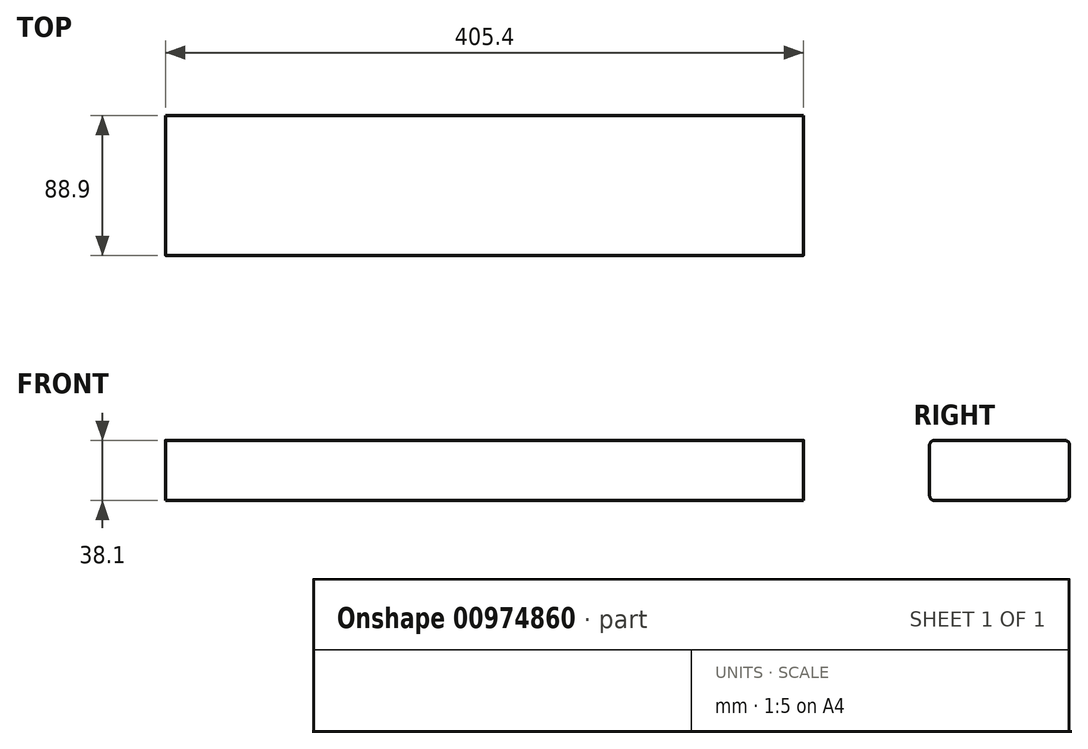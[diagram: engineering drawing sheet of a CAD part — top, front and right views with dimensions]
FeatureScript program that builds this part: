
annotation { "Feature Type Name" : "Feature", "Feature Type Description" : "" }
export const myFeature = defineFeature(function(context is Context, id is Id, definition is map)
    precondition{}
    {
        {
            var Q0;
            Q0=qCreatedBy(makeId("Top.planeOp"),FACE);
            var sketch = newSketch(context, id + "F0", { "sketchPlane" : qUnion([Q0])});
            skLineSegment(sketch, "E0.bottom", {"start": v(202.7, 44.45) * mm, "end": v(-202.7, 44.45) * mm});
            skLineSegment(sketch, "E0.top", {"start": v(202.7, -44.45) * mm, "end": v(-202.7, -44.45) * mm});
            skLineSegment(sketch, "E0.left", {"start": v(202.7, 44.45) * mm, "end": v(202.7, -44.45) * mm});
            skLineSegment(sketch, "E0.right", {"start": v(-202.7, 44.45) * mm, "end": v(-202.7, -44.45) * mm});
            skPoint(sketch, "E0.middle", {"position": v(0, 0) * mm});
            skSolve(sketch);
        }
        {
            var Q0;
            Q0=makeQuery(id+"F0.imprint","IMPRINT",FACE,{"disambiguationData":[TD([[makeQuery(id+"F0.imprint","IMPRINT",EDGE,{"derivedFrom":sQuery(id+"F0.wireOp",EDGE,"E0.bottom")}),1.0]])]});
            extrude(context, id + "F1", {"entities" : qUnion([Q0]), "depth" : 38.1 * mm, "offsetDistance" : 25 * mm});
        }
        {
            var Q0;
            Q0=makeQuery(id+"F1.opExtrude","CAP_EDGE",EDGE,{"disambiguationData":[OSD([sQuery(id+"F0.wireOp",EDGE,"E0.top")])],"isStart":false});
            var Q1;
            Q1=makeQuery(id+"F1.opExtrude","CAP_EDGE",EDGE,{"disambiguationData":[OSD([sQuery(id+"F0.wireOp",EDGE,"E0.top")])],"isStart":true});
            var Q2;
            Q2=makeQuery(id+"F1.opExtrude","CAP_EDGE",EDGE,{"disambiguationData":[OSD([sQuery(id+"F0.wireOp",EDGE,"E0.bottom")])],"isStart":false});
            var Q3;
            Q3=makeQuery(id+"F1.opExtrude","CAP_EDGE",EDGE,{"disambiguationData":[OSD([sQuery(id+"F0.wireOp",EDGE,"E0.bottom")])],"isStart":true});
            fillet(context, id + "F2", {"entities" : qUnion([Q0, Q1, Q2, Q3]), "radius" : 3 * mm, "tangentPropagation" : true, "allowEdgeOverflow" : false});
        }
    });
